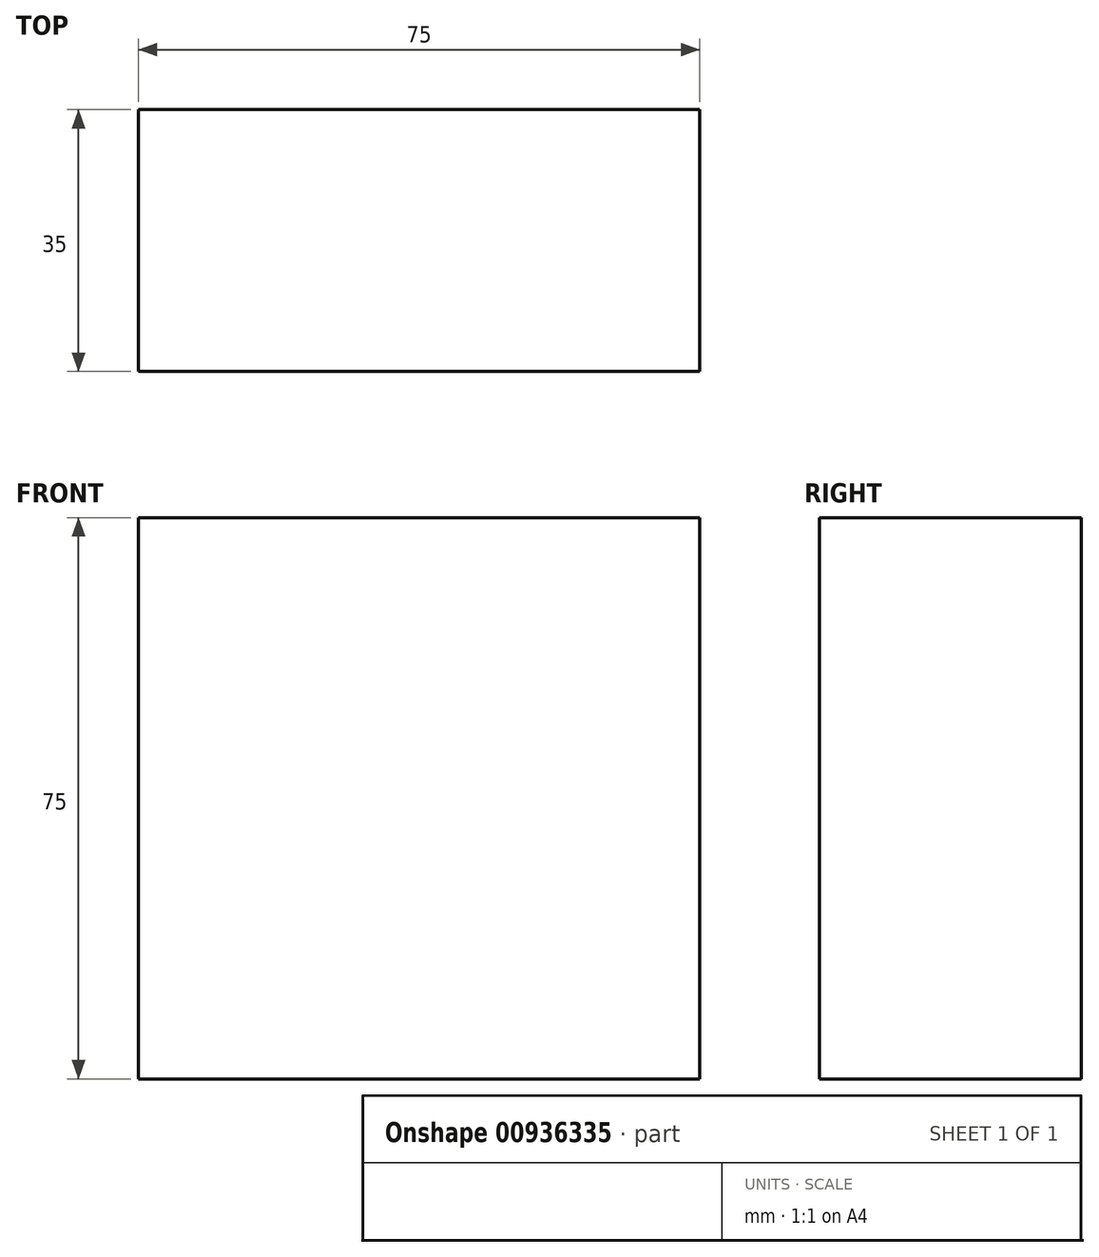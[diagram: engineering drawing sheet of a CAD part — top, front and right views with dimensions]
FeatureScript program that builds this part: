
annotation { "Feature Type Name" : "Feature", "Feature Type Description" : "" }
export const myFeature = defineFeature(function(context is Context, id is Id, definition is map)
    precondition{}
    {
        {
            var Q0;
            Q0=qCreatedBy(makeId("Front.planeOp"),FACE);
            var sketch = newSketch(context, id + "F0", { "sketchPlane" : qUnion([Q0])});
            skLineSegment(sketch, "E0", {"start": v(0, 0) * mm, "end": v(20, 0) * mm});
            skLineSegment(sketch, "E1", {"start": v(20, 0) * mm, "end": v(20, 50) * mm});
            skLineSegment(sketch, "E2", {"start": v(20, 50) * mm, "end": v(-55, 50) * mm});
            skLineSegment(sketch, "E3", {"start": v(-55, 50) * mm, "end": v(-55, 0) * mm});
            skLineSegment(sketch, "E4", {"start": v(-55, 0) * mm, "end": v(0, 0) * mm});
            skSolve(sketch);
        }
        {
            var Q0;
            Q0=makeQuery(id+"F0.imprint","IMPRINT",FACE,{"disambiguationData":[TD([[makeQuery(id+"F0.imprint","IMPRINT",EDGE,{"derivedFrom":sQuery(id+"F0.wireOp",EDGE,"E0")}),1.0]])]});
            extrude(context, id + "F1", {"entities" : qUnion([Q0]), "depth" : 20 * mm, "offsetDistance" : 25 * mm});
        }
        {
            var Q0;
            Q0=makeQuery(id+"F1.opExtrude","CAP_FACE",FACE,{"disambiguationData":[OSD([sQuery(id+"F0.wireOp",EDGE,"E0"),sQuery(id+"F0.wireOp",EDGE,"E1"),sQuery(id+"F0.wireOp",EDGE,"E2"),sQuery(id+"F0.wireOp",EDGE,"E3"),sQuery(id+"F0.wireOp",EDGE,"E4")])],"isStart":true});
            extrude(context, id + "F2", {"entities" : qUnion([Q0]), "operationType" : NewBodyOperationType.ADD, "depth" : 15 * mm, "offsetDistance" : 25 * mm});
        }
        {
            var Q0;
            {var subQ0=sQuery(id+"F0.wireOp",EDGE,"E4");var subQ1=sQuery(id+"F0.wireOp",EDGE,"E0");Q0=makeQuery(id+"F2.boolean.opBoolean","MERGE",FACE,{"derivedFrom":[makeQuery(id+"F1.opExtrude","SWEPT_FACE",FACE,{"disambiguationData":[OSD([subQ1,subQ0])]}),makeQuery(id+"F2.opExtrude","SWEPT_FACE",FACE,{"disambiguationData":[OSD([subQ1,subQ0])]})]});}
            var sketch = newSketch(context, id + "F3", { "sketchPlane" : qUnion([Q0])});
            skSolve(sketch);
        }
        {
            var Q0;
            {var subQ0=sQuery(id+"F0.wireOp",EDGE,"E4");var subQ1=sQuery(id+"F0.wireOp",EDGE,"E0");Q0=makeQuery(id+"F3.imprint","IMPRINT",FACE,{"disambiguationData":[TD([[makeQuery(id+"F3.imprint","IMPRINT",EDGE,{"derivedFrom":makeQuery(id+"F1.opExtrude","CAP_EDGE",EDGE,{"disambiguationData":[OSD([subQ1,subQ0])],"isStart":false})}),-1.0]])]});}
            extrude(context, id + "F4", {"entities" : qUnion([Q0]), "operationType" : NewBodyOperationType.ADD, "depth" : 25 * mm, "offsetDistance" : 25 * mm});
        }
    });
